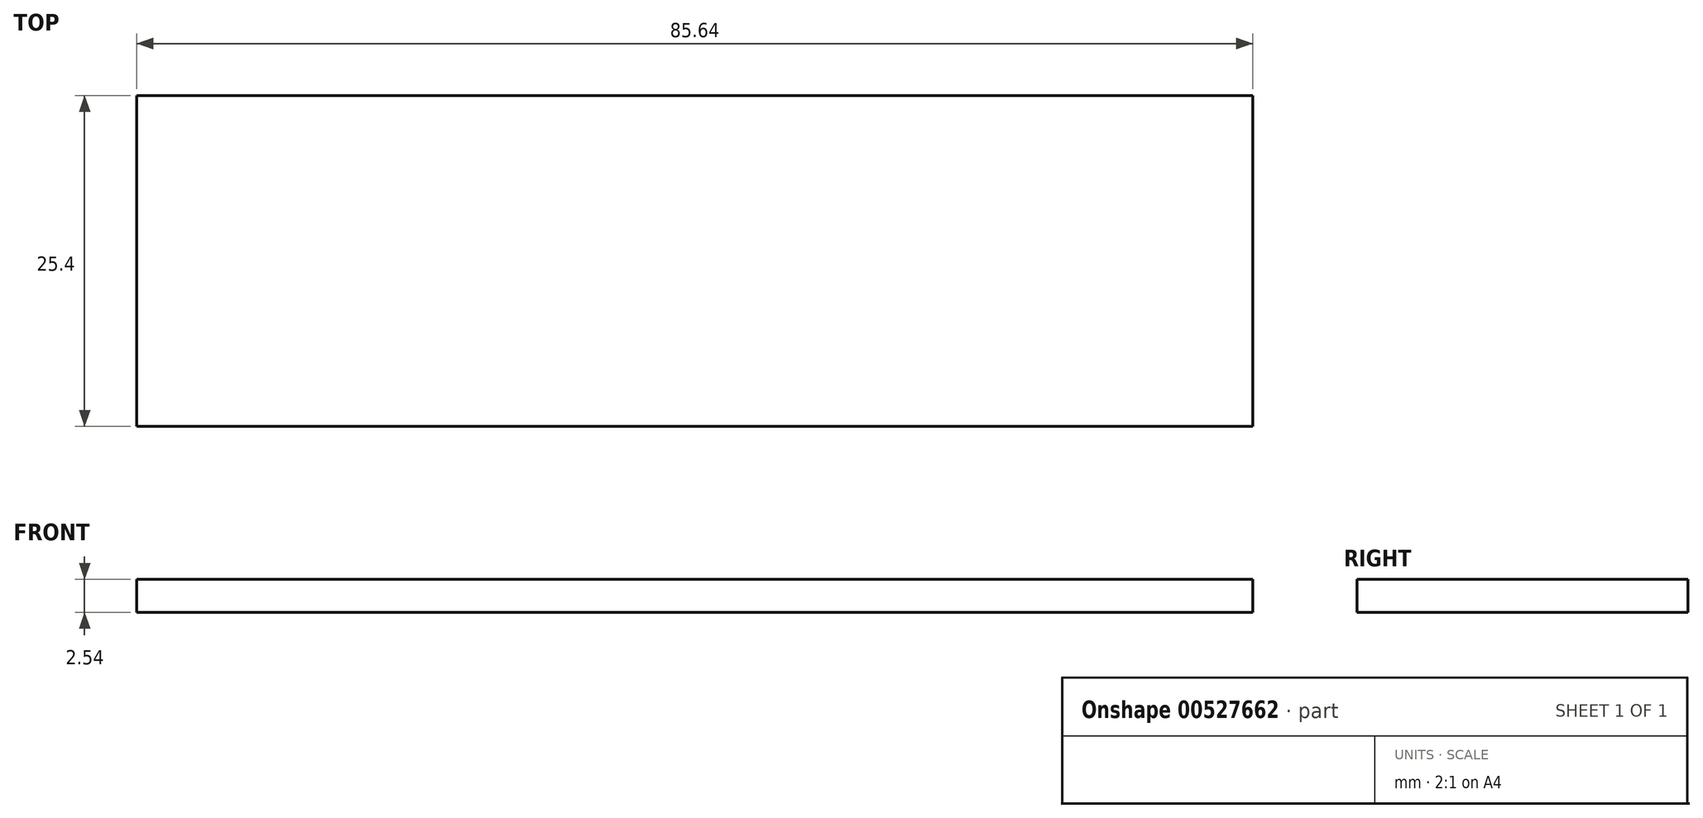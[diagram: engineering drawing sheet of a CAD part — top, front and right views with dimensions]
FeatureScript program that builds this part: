
annotation { "Feature Type Name" : "Feature", "Feature Type Description" : "" }
export const myFeature = defineFeature(function(context is Context, id is Id, definition is map)
    precondition{}
    {
        {
            var Q0;
            Q0=qCreatedBy(makeId("Front.planeOp"),FACE);
            var sketch = newSketch(context, id + "F0", { "sketchPlane" : qUnion([Q0])});
            skLineSegment(sketch, "E0.bottom", {"start": v(-42.82, -1.55) * mm, "end": v(42.82, -1.55) * mm});
            skLineSegment(sketch, "E0.top", {"start": v(-42.82, -2.8) * mm, "end": v(42.82, -2.8) * mm});
            skLineSegment(sketch, "E0.left", {"start": v(-42.82, -1.55) * mm, "end": v(-42.82, -2.8) * mm});
            skLineSegment(sketch, "E0.right", {"start": v(42.82, -1.55) * mm, "end": v(42.82, -2.8) * mm});
            skSolve(sketch);
        }
        {
            var Q0;
            Q0=sQuery(id+"F0.wireOp",EDGE,"E0.bottom");
            var Q1;
            Q1=sQuery(id+"F0.wireOp",EDGE,"E0.left");
            extrude(context, id + "F1", {"bodyType" : ToolBodyType.SURFACE, "surfaceEntities" : qUnion([Q0, Q1]), "depth" : 25.4 * mm, "offsetDistance" : 25.4 * mm});
        }
        {
            var Q0;
            Q0=makeQuery(id+"F1.opExtrude","SWEPT_FACE",FACE,{"disambiguationData":[OSD([sQuery(id+"F0.wireOp",EDGE,"E0.bottom")])]});
            extrude(context, id + "F2", {"entities" : qUnion([Q0]), "depth" : 2.54 * mm, "offsetDistance" : 25.4 * mm});
        }
    });
